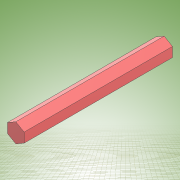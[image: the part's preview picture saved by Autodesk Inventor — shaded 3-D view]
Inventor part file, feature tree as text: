
AUTODESK INVENTOR PART (.ipt)
format: ipt  version: 2022 (Build 260153000, 153)  size: 117,760 bytes
history: native  units: mm
features: other x1, extrude x1, sketch x1
ambient origin geometry x8: Origin, YZ Plane, XZ Plane, XY Plane, X Axis, Y Axis, Z Axis, Center Point
bodies: Body1 (feature_tree)
feature tree (3):
  other  "Sólido1"
  extrude  "Extrusión1"  Depth=50.0mm TaperAngle=0.0deg
  sketch  "Boceto1"  dims[d0=5.6mm d1=50.0mm d2=0.0mm]
